# Revit family: NEW F5 preto
name_source: partatom
category: Equipamento especial
revit_build: Autodesk Revit 2016 (Build: 20150220_1215(x64)
units: mm (PartAtom-declared; Revit-internal decimal feet)

## family parameters
Com base no plano de trabalho = Não
Compartilhado = Não
Corte com vazios quando carregados = Não
Cota do conector redondo = Utilizar diâmetro
Ponto de cálculo do ambiente = Não
Sempre na vertical = Sim
Tipo de parte = Normal

## types (1)
- Tramontina Forno Elétrico -94867/220
    Classe de Construção = Classe I
    Código de montagem = 94867/220
    Descrição = 94867/220
    Desenvolvedor = Factory Cursos & Desenvolvimento
    Disjuntor termomagnético = 16 A
    Fabricante = Tramontina
    Frequência = 60 Hz
    Grau de proteção = IPX0
    Intensidade da corrente elétrica = 10 A
    Modelo = New Glass Cook B60 F5+
    Nicho para instalação (AxLxP) = 590 X 560 X 600
    Peso Bruto = 38,8 kg
    Peso liquido = 33,4 kg
    Potência "Aquecimento Inferior" = 1100 W
    Potência "Aquecimento superior" = 2000 MHz
    Potência "Assar Combinado" = 2100 W
    Potência "Assar" = 2100 W
    Potência "Booster" = 2100 W
    Potência "Lâmpada do forno" = 25 W
    Potência "Turbo Grill" = 1000 W
    Potência Elétrica total = 2100 W
    Site do desenvolvedor = www.factorycursos.com.br
    Tensão = 220 V
    URL = www.tramontina.com.br
    Volume líquido = 71 L
